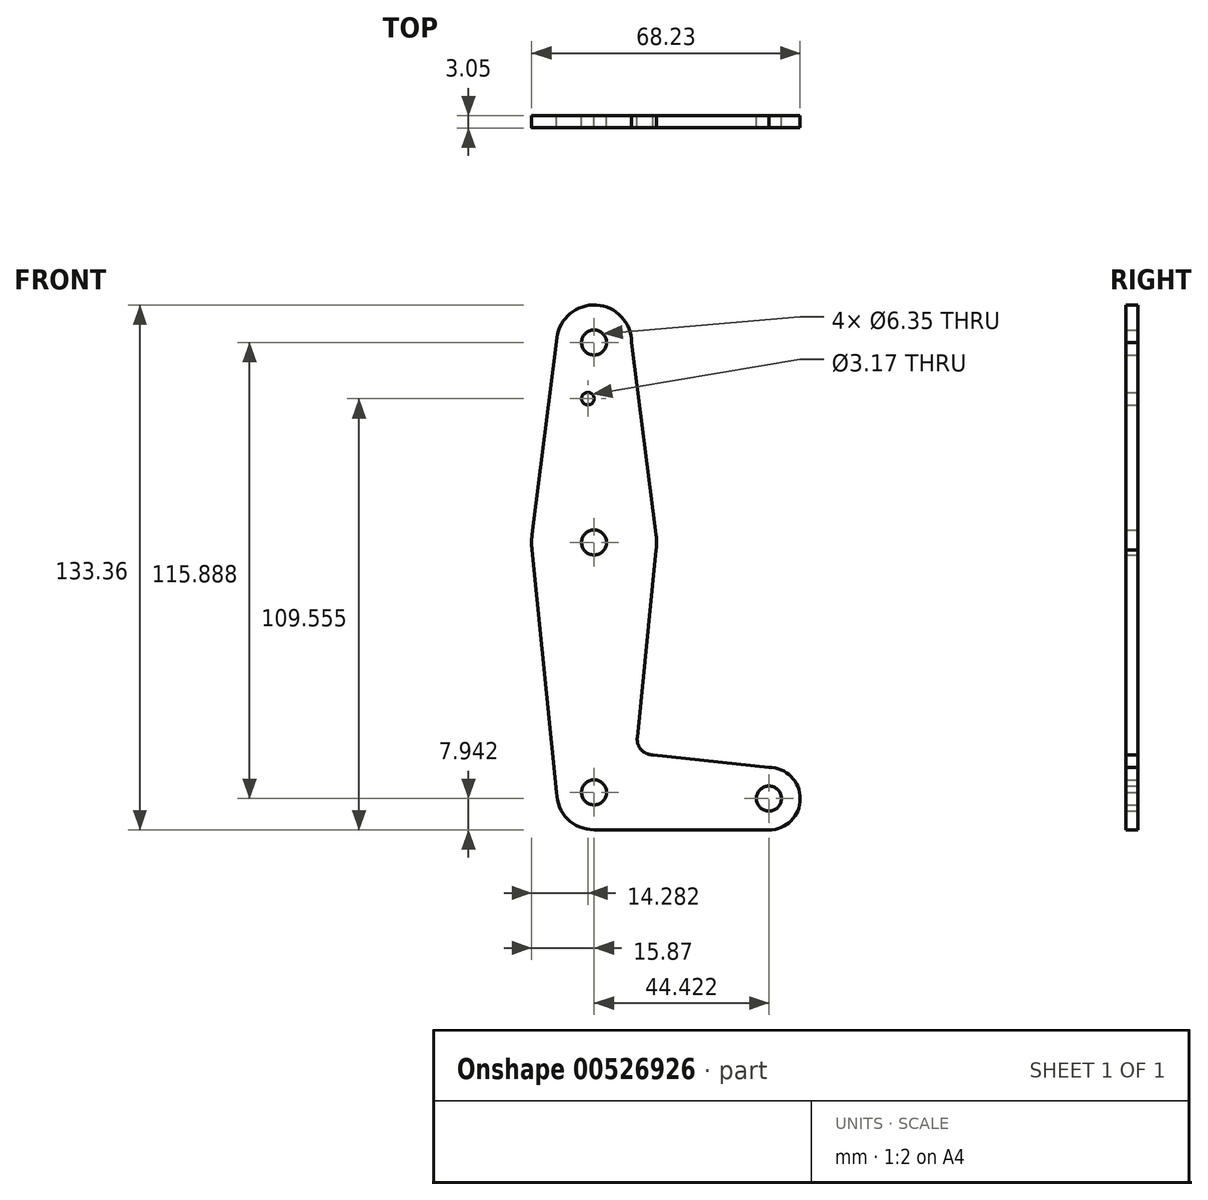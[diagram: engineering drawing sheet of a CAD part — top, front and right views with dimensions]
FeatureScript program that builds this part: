
annotation { "Feature Type Name" : "Feature", "Feature Type Description" : "" }
export const myFeature = defineFeature(function(context is Context, id is Id, definition is map)
    precondition{}
    {
        {
            var Q0;
            Q0=qCreatedBy(makeId("Front.planeOp"),FACE);
            var sketch = newSketch(context, id + "F0", { "sketchPlane" : qUnion([Q0])});
            skLineSegment(sketch, "E0", {"start": v(0, 0) * mm, "end": v(0, 114.3) * mm, "construction": true});
            skCircle(sketch, "E1", {"center": v(0, 0) * mm, "radius": 9.53 * mm});
            skCircle(sketch, "E2", {"center": v(0, 114.3) * mm, "radius": 9.53 * mm});
            skLineSegment(sketch, "E3", {"start": v(0, 0) * mm, "end": v(44.42, -1.59) * mm, "construction": true});
            skCircle(sketch, "E4", {"center": v(44.42, -1.59) * mm, "radius": 7.94 * mm});
            skLineSegment(sketch, "E5", {"start": v(0, 0) * mm, "end": v(0, 63.5) * mm});
            skCircle(sketch, "E6", {"center": v(0, 63.5) * mm, "radius": 15.88 * mm});
            skLineSegment(sketch, "E7", {"start": v(-9.45, 115.5) * mm, "end": v(-15.75, 65.48) * mm});
            skLineSegment(sketch, "E8", {"start": v(9.53, 114.3) * mm, "end": v(15.75, 65.48) * mm});
            skLineSegment(sketch, "E9", {"start": v(44.84, -9.52) * mm, "end": v(0, -9.53) * mm});
            skLineSegment(sketch, "E10", {"start": v(15.75, 61.52) * mm, "end": v(10.95, 13.71) * mm});
            skLineSegment(sketch, "E11", {"start": v(0, 63.5) * mm, "end": v(0, 100.03) * mm});
            skCircle(sketch, "E12", {"center": v(-1.59, 100.03) * mm, "radius": 1.59 * mm});
            skCircle(sketch, "E13", {"center": v(0, 63.5) * mm, "radius": 3.18 * mm});
            skCircle(sketch, "E14", {"center": v(0, 0) * mm, "radius": 3.18 * mm});
            skCircle(sketch, "E15", {"center": v(0, 114.3) * mm, "radius": 3.18 * mm});
            skCircle(sketch, "E16", {"center": v(44.42, -1.59) * mm, "radius": 3.18 * mm});
            skArc(sketch, "E17", {"start": v(10.95, 13.71) * mm, "mid": v(10.9, 13.35) * mm, "end": v(10.88, 12.99) * mm});
            skLineSegment(sketch, "E18.trimOffspring", {"start": v(9.57, 0) * mm, "end": v(9.54, -0.34) * mm});
            skArc(sketch, "E19", {"start": v(11.16, 14.76) * mm, "mid": v(12, 10.81) * mm, "end": v(15.86, 9.64) * mm});
            skPoint(sketch, "E19.first.point", {"position": v(18.18, 15.78) * mm});
            skPoint(sketch, "E19.second.point", {"position": v(15.86, 9.64) * mm});
            skPoint(sketch, "E19.third.point", {"position": v(11.16, 14.76) * mm});
            skLineSegment(sketch, "E20.trimOffspring", {"start": v(14.92, 9.53) * mm, "end": v(44.42, 6.35) * mm});
            skPoint(sketch, "E21.start.orphan", {"position": v(0, 9.53) * mm});
            skLineSegment(sketch, "E22", {"start": v(-9.53, 0) * mm, "end": v(-15.75, 61.52) * mm});
            skSolve(sketch);
        }
        {
            var Q0;
            Q0 = qSketchRegion(id + "F0", true);
            extrude(context, id + "F1", {"entities" : qUnion([Q0]), "depth" : 3.05 * mm, "offsetDistance" : 25.4 * mm});
        }
    });
